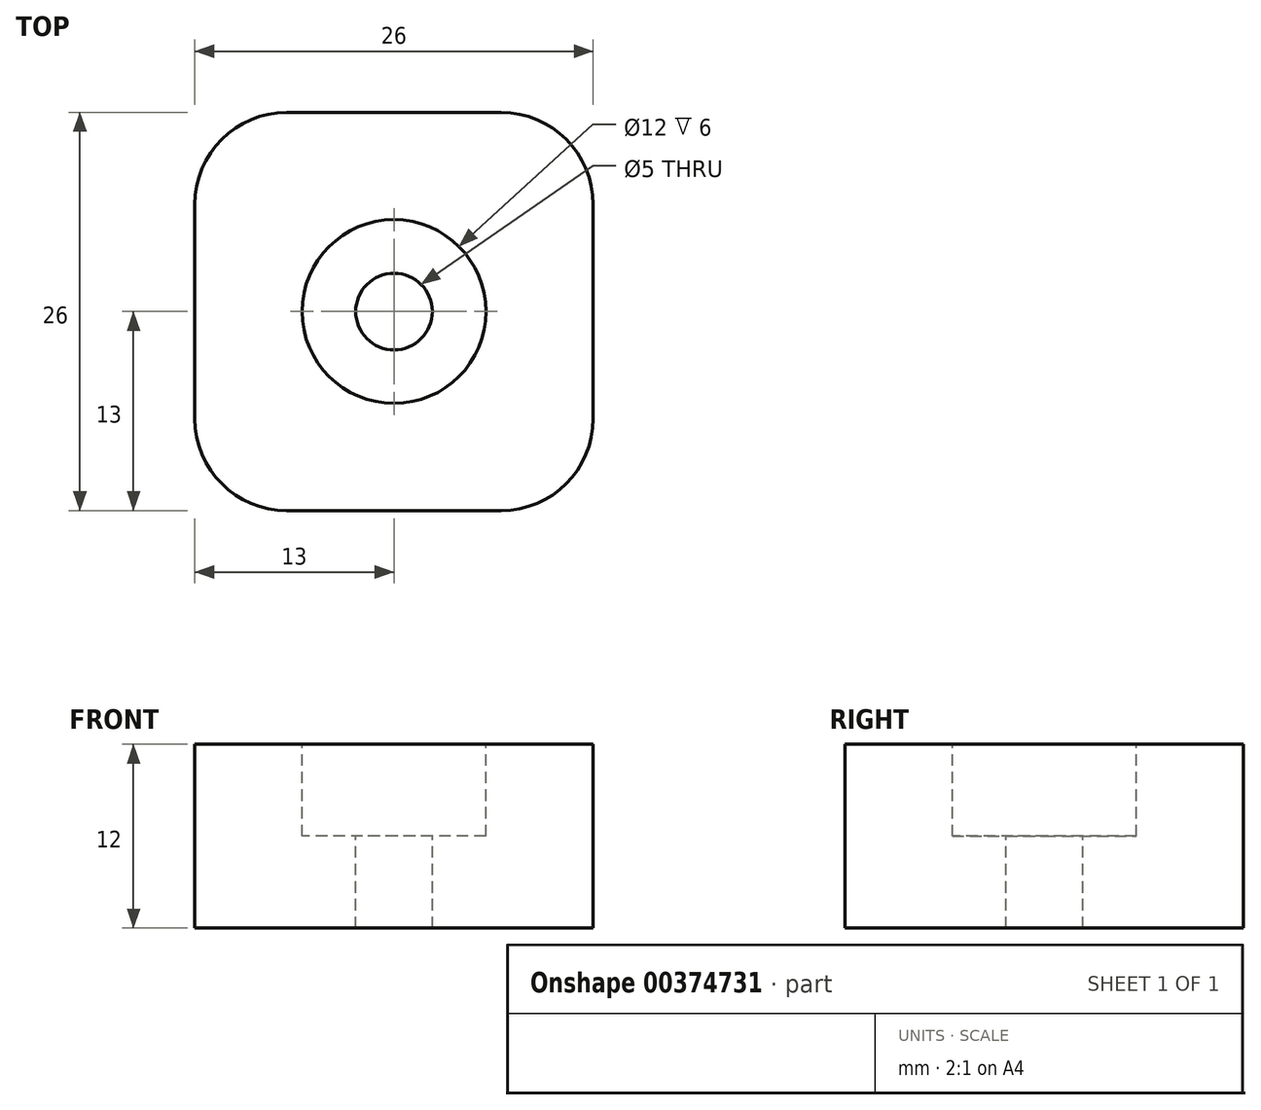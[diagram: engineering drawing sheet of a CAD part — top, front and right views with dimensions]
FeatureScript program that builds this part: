
annotation { "Feature Type Name" : "Feature", "Feature Type Description" : "" }
export const myFeature = defineFeature(function(context is Context, id is Id, definition is map)
    precondition{}
    {
        {
            var Q0;
            Q0=qCreatedBy(makeId("Top.planeOp"),FACE);
            var sketch = newSketch(context, id + "F0", { "sketchPlane" : qUnion([Q0])});
            skLineSegment(sketch, "E0.bottom", {"start": v(7, -13) * mm, "end": v(-7, -13) * mm});
            skLineSegment(sketch, "E0.top", {"start": v(7, 13) * mm, "end": v(-7, 13) * mm});
            skLineSegment(sketch, "E0.left", {"start": v(13, -7) * mm, "end": v(13, 7) * mm});
            skLineSegment(sketch, "E0.right", {"start": v(-13, -7) * mm, "end": v(-13, 7) * mm});
            skPoint(sketch, "E0.middle", {"position": v(0, 0) * mm});
            skPoint(sketch, "E1.visualSharp", {"position": v(-13, 13) * mm});
            skArc(sketch, "E1.filletArc", {"start": v(-7, 13) * mm, "mid": v(-11.24, 11.24) * mm, "end": v(-13, 7) * mm});
            skPoint(sketch, "E2.visualSharp", {"position": v(-13, -13) * mm});
            skArc(sketch, "E2.filletArc", {"start": v(-13, -7) * mm, "mid": v(-11.24, -11.24) * mm, "end": v(-7, -13) * mm});
            skPoint(sketch, "E3.visualSharp", {"position": v(13, 13) * mm});
            skArc(sketch, "E3.filletArc", {"start": v(13, 7) * mm, "mid": v(11.24, 11.24) * mm, "end": v(7, 13) * mm});
            skPoint(sketch, "E4.visualSharp", {"position": v(13, -13) * mm});
            skArc(sketch, "E4.filletArc", {"start": v(7, -13) * mm, "mid": v(11.24, -11.24) * mm, "end": v(13, -7) * mm});
            skSolve(sketch);
        }
        {
            var Q0;
            Q0 = qSketchRegion(id + "F0", true);
            extrude(context, id + "F1", {"entities" : qUnion([Q0]), "depth" : 12 * mm});
        }
        {
            var Q0;
            Q0=makeQuery(id+"F1.opExtrude","CAP_FACE",FACE,{"disambiguationData":[OSD([sQuery(id+"F0.wireOp",EDGE,"E0.bottom"),sQuery(id+"F0.wireOp",EDGE,"E0.top"),sQuery(id+"F0.wireOp",EDGE,"E0.left"),sQuery(id+"F0.wireOp",EDGE,"E0.right"),sQuery(id+"F0.wireOp",EDGE,"E1.filletArc"),sQuery(id+"F0.wireOp",EDGE,"E2.filletArc"),sQuery(id+"F0.wireOp",EDGE,"E3.filletArc"),sQuery(id+"F0.wireOp",EDGE,"E4.filletArc")])],"isStart":false});
            var sketch = newSketch(context, id + "F2", { "sketchPlane" : qUnion([Q0])});
            skCircle(sketch, "E5", {"center": v(0, 0) * mm, "radius": 6 * mm});
            skSolve(sketch);
        }
        {
            var Q0;
            Q0 = qSketchRegion(id + "F2", true);
            extrude(context, id + "F3", {"entities" : qUnion([Q0]), "operationType" : NewBodyOperationType.REMOVE, "oppositeDirection" : true, "depth" : 6 * mm});
        }
        {
            var Q0;
            Q0=makeQuery(id+"F3.boolean.opBoolean","COPY",FACE,{"derivedFrom":makeQuery(id+"F3.opExtrude","CAP_FACE",FACE,{"disambiguationData":[OSD([sQuery(id+"F2.wireOp",EDGE,"E5")])],"isStart":false})});
            var sketch = newSketch(context, id + "F4", { "sketchPlane" : qUnion([Q0])});
            skCircle(sketch, "E6", {"center": v(0, 0) * mm, "radius": 2.5 * mm});
            skSolve(sketch);
        }
        {
            var Q0;
            Q0 = qSketchRegion(id + "F4", true);
            extrude(context, id + "F5", {"entities" : qUnion([Q0]), "operationType" : NewBodyOperationType.REMOVE, "oppositeDirection" : true, "depth" : 31.5 * mm});
        }
    });
